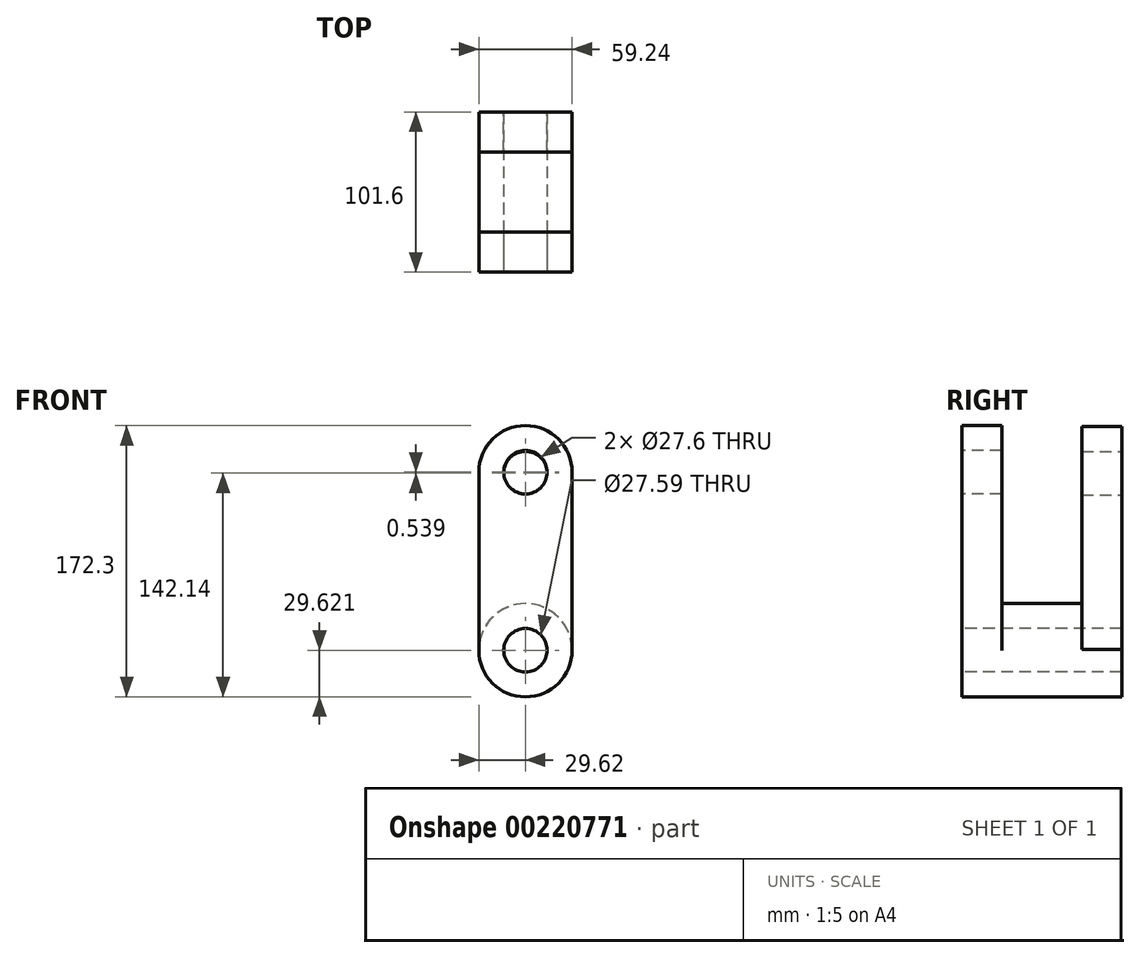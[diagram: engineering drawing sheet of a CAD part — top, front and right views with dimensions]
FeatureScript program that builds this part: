
annotation { "Feature Type Name" : "Feature", "Feature Type Description" : "" }
export const myFeature = defineFeature(function(context is Context, id is Id, definition is map)
    precondition{}
    {
        {
            var Q0;
            Q0=qCreatedBy(makeId("Front.planeOp"),FACE);
            var sketch = newSketch(context, id + "F0", { "sketchPlane" : qUnion([Q0])});
            skLineSegment(sketch, "E0.left", {"start": v(29.62, -56.53) * mm, "end": v(29.62, 56.53) * mm});
            skLineSegment(sketch, "E0.right", {"start": v(-29.62, -56.53) * mm, "end": v(-29.62, 56.53) * mm});
            skPoint(sketch, "E0.middle", {"position": v(0, 0) * mm});
            skArc(sketch, "E1", {"start": v(29.62, 56.53) * mm, "mid": v(0, 86.15) * mm, "end": v(-29.62, 56.53) * mm});
            skArc(sketch, "E2", {"start": v(29.62, -56.53) * mm, "mid": v(0, -26.91) * mm, "end": v(-29.62, -56.53) * mm});
            skCircle(sketch, "E3", {"center": v(0, 56.53) * mm, "radius": 13.8 * mm});
            skSolve(sketch);
        }
        {
            var Q0;
            {var subQ1=sQuery(id+"F0.wireOp",EDGE,"E0.left");Q0=makeQuery(id+"F0.imprint","IMPRINT",FACE,{"disambiguationData":[TD([[makeQuery(id+"F0.imprint","IMPRINT",EDGE,{"derivedFrom":subQ1}),1.0]])]});}
            extrude(context, id + "F1", {"entities" : qUnion([Q0]), "oppositeDirection" : true, "depth" : 25.4 * mm});
        }
        {
            var Q0;
            Q0=makeQuery(id+"F1.opExtrude","CAP_FACE",FACE,{"disambiguationData":[OSD([sQuery(id+"F0.wireOp",EDGE,"E0.left"),sQuery(id+"F0.wireOp",EDGE,"E0.right"),sQuery(id+"F0.wireOp",EDGE,"E1"),sQuery(id+"F0.wireOp",EDGE,"E2"),sQuery(id+"F0.wireOp",EDGE,"E3")])],"isStart":true});
            var sketch = newSketch(context, id + "F2", { "sketchPlane" : qUnion([Q0])});
            skCircle(sketch, "E4", {"center": v(0, -56.53) * mm, "radius": 29.62 * mm});
            skCircle(sketch, "E5", {"center": v(0, -56.53) * mm, "radius": 13.8 * mm});
            skSolve(sketch);
        }
        {
            var Q0;
            Q0 = qSketchRegion(id + "F2", true);
            extrude(context, id + "F3", {"entities" : qUnion([Q0]), "operationType" : NewBodyOperationType.ADD, "oppositeDirection" : true, "depth" : 101.6 * mm});
        }
        {
            var Q0;
            Q0=makeQuery(id+"F3.opExtrude","CAP_FACE",FACE,{"disambiguationData":[OSD([sQuery(id+"F2.wireOp",EDGE,"E4"),sQuery(id+"F2.wireOp",EDGE,"E5")])],"isStart":false});
            var sketch = newSketch(context, id + "F4", { "sketchPlane" : qUnion([Q0])});
            skLineSegment(sketch, "E6.left", {"start": v(29.61, -56) * mm, "end": v(29.61, 56) * mm});
            skLineSegment(sketch, "E6.right", {"start": v(-29.61, -56) * mm, "end": v(-29.61, 56) * mm});
            skPoint(sketch, "E6.middle", {"position": v(0, 0) * mm});
            skArc(sketch, "E7", {"start": v(29.61, 56) * mm, "mid": v(0, 85.6) * mm, "end": v(-29.61, 56) * mm});
            skCircle(sketch, "E8", {"center": v(0, 56) * mm, "radius": 13.8 * mm});
            skSolve(sketch);
        }
        {
            var Q0;
            {var subQ1=sQuery(id+"F4.wireOp",EDGE,"E6.left");Q0=makeQuery(id+"F4.imprint","IMPRINT",FACE,{"disambiguationData":[TD([[makeQuery(id+"F4.imprint","IMPRINT",EDGE,{"derivedFrom":subQ1}),1.0]])]});}
            var Q1;
            Q1=sQuery(id+"F4.wireOp",EDGE,"E6.left");
            var Q2;
            Q2=sQuery(id+"F4.wireOp",EDGE,"E7");
            var Q3;
            Q3=sQuery(id+"F4.wireOp",EDGE,"E6.right");
            extrude(context, id + "F5", {"entities" : qUnion([Q0]), "operationType" : NewBodyOperationType.ADD, "surfaceEntities" : qUnion([Q1, Q2, Q3]), "oppositeDirection" : true, "depth" : 25.4 * mm});
        }
    });
